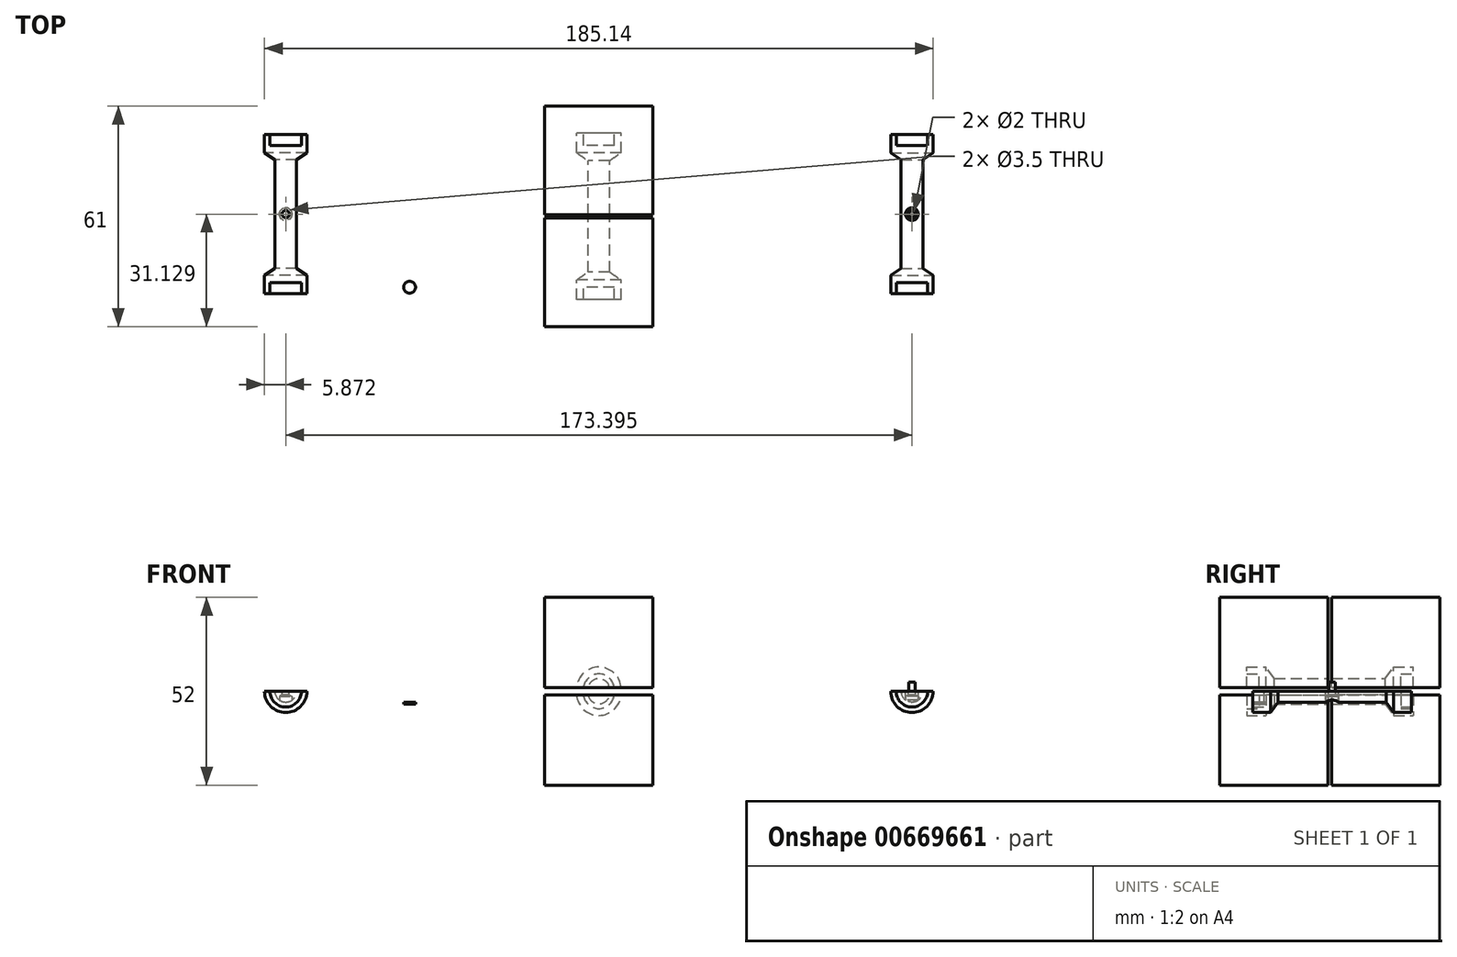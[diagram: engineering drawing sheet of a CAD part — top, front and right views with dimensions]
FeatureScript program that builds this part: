
annotation { "Feature Type Name" : "Feature", "Feature Type Description" : "" }
export const myFeature = defineFeature(function(context is Context, id is Id, definition is map)
    precondition{}
    {
        {
            var Q0;
            Q0=qCreatedBy(makeId("Top.planeOp"),FACE);
            var sketch = newSketch(context, id + "F0", { "sketchPlane" : qUnion([Q0])});
            skLineSegment(sketch, "E0", {"start": v(0, 71.15) * mm, "end": v(0, -54.04) * mm});
            skLineSegment(sketch, "E1", {"start": v(0, -54.04) * mm, "end": v(0, 71.15) * mm});
            skLineSegment(sketch, "E2", {"start": v(-3, 0) * mm, "end": v(-3, 15.4) * mm});
            skLineSegment(sketch, "E3", {"start": v(-3, 15.4) * mm, "end": v(-6.2, 17.63) * mm});
            skLineSegment(sketch, "E4", {"start": v(-6.2, 17.63) * mm, "end": v(-6.2, 23.03) * mm});
            skLineSegment(sketch, "E5", {"start": v(-6.2, 23.03) * mm, "end": v(-4.3, 23.03) * mm});
            skLineSegment(sketch, "E6", {"start": v(-4.3, 23.03) * mm, "end": v(-4.3, 19.63) * mm});
            skLineSegment(sketch, "E7", {"start": v(-4.3, 19.63) * mm, "end": v(0, 19.63) * mm});
            skLineSegment(sketch, "E8", {"start": v(0, 19.63) * mm, "end": v(0, 0) * mm});
            skLineSegment(sketch, "E9", {"start": v(0, 0) * mm, "end": v(-3, 0) * mm});
            skLineSegment(sketch, "E10.MirrorCS", {"start": v(-6.2, -23.03) * mm, "end": v(-4.3, -23.03) * mm});
            skLineSegment(sketch, "E11.MirrorCS", {"start": v(-3, -15.4) * mm, "end": v(-6.2, -17.63) * mm});
            skLineSegment(sketch, "E12.MirrorCS", {"start": v(-4.3, -23.03) * mm, "end": v(-4.3, -19.63) * mm});
            skLineSegment(sketch, "E13.MirrorCS", {"start": v(0, -19.63) * mm, "end": v(0, 0) * mm});
            skLineSegment(sketch, "E14.MirrorCS", {"start": v(-4.3, -19.63) * mm, "end": v(0, -19.63) * mm});
            skLineSegment(sketch, "E15.MirrorCS", {"start": v(-6.2, -17.63) * mm, "end": v(-6.2, -23.03) * mm});
            skLineSegment(sketch, "E16.MirrorCS", {"start": v(-3, 0) * mm, "end": v(-3, -15.4) * mm});
            skLineSegment(sketch, "E17", {"start": v(-89.7, 0.63) * mm, "end": v(-89.7, 15.63) * mm});
            skLineSegment(sketch, "E18", {"start": v(-89.7, 15.63) * mm, "end": v(-92.57, 17.63) * mm});
            skLineSegment(sketch, "E19", {"start": v(-92.57, 17.63) * mm, "end": v(-92.57, 22.63) * mm});
            skLineSegment(sketch, "E20", {"start": v(-92.57, 22.63) * mm, "end": v(-91.07, 22.63) * mm});
            skLineSegment(sketch, "E21", {"start": v(-91.07, 22.63) * mm, "end": v(-91.07, 19.63) * mm});
            skLineSegment(sketch, "E22", {"start": v(-91.07, 19.63) * mm, "end": v(-86.7, 19.63) * mm});
            skLineSegment(sketch, "E23", {"start": v(-86.7, 19.63) * mm, "end": v(-86.7, 0.63) * mm});
            skLineSegment(sketch, "E24", {"start": v(-86.7, 0.63) * mm, "end": v(-89.7, 0.63) * mm});
            skLineSegment(sketch, "E25.MirrorCS", {"start": v(-92.57, -21.37) * mm, "end": v(-91.07, -21.37) * mm});
            skLineSegment(sketch, "E26.MirrorCS", {"start": v(-89.7, -14.37) * mm, "end": v(-92.57, -16.37) * mm});
            skLineSegment(sketch, "E27.MirrorCS", {"start": v(-91.07, -21.37) * mm, "end": v(-91.07, -18.37) * mm});
            skLineSegment(sketch, "E28.MirrorCS", {"start": v(-92.57, -16.37) * mm, "end": v(-92.57, -21.37) * mm});
            skLineSegment(sketch, "E29.MirrorCS", {"start": v(-86.7, -18.37) * mm, "end": v(-86.7, 0.63) * mm});
            skLineSegment(sketch, "E30.MirrorCS", {"start": v(-91.07, -18.37) * mm, "end": v(-86.7, -18.37) * mm});
            skLineSegment(sketch, "E31.MirrorCS", {"start": v(-89.7, 0.63) * mm, "end": v(-89.7, -14.37) * mm});
            skSolve(sketch);
        }
        {
            var Q0;
            Q0=makeQuery(id+"F0.imprint","IMPRINT",FACE,{"disambiguationData":[TD([[makeQuery(id+"F0.imprint","IMPRINT",EDGE,{"derivedFrom":sQuery(id+"F0.wireOp",EDGE,"E2")}),-1.0]])]});
            var Q1;
            Q1=makeQuery(id+"F0.imprint","IMPRINT",FACE,{"disambiguationData":[TD([[makeQuery(id+"F0.imprint","IMPRINT",EDGE,{"derivedFrom":sQuery(id+"F0.wireOp",EDGE,"E10.MirrorCS")}),1.0]])]});
            var Q2;
            Q2=sQuery(id+"F0.wireOp",EDGE,"E8");
            revolve(context, id + "F1", {"entities" : qUnion([Q0, Q1]), "axis" : qUnion([Q2]), "revolveType" : RevolveType.ONE_DIRECTION, "angle" : 180 * degree});
        }
        {
            var Q0;
            Q0=qCreatedBy(makeId("Right.planeOp"),FACE);
            var sketch = newSketch(context, id + "F2", { "sketchPlane" : qUnion([Q0])});
            skLineSegment(sketch, "E32.bottom", {"start": v(30, -25) * mm, "end": v(0, -25) * mm});
            skLineSegment(sketch, "E32.top", {"start": v(30, -50) * mm, "end": v(0, -50) * mm});
            skLineSegment(sketch, "E32.left", {"start": v(30, -25) * mm, "end": v(30, -50) * mm});
            skLineSegment(sketch, "E32.right", {"start": v(0, -25) * mm, "end": v(0, -50) * mm});
            skSolve(sketch);
        }
        {
            var Q0;
            Q0=makeQuery(id+"F2.imprint","IMPRINT",FACE,{"disambiguationData":[TD([[makeQuery(id+"F2.imprint","IMPRINT",EDGE,{"derivedFrom":sQuery(id+"F2.wireOp",EDGE,"E32.bottom")}),1.0]])]});
            extrude(context, id + "F3", {"entities" : qUnion([Q0]), "depth" : 15 * mm, "offsetDistance" : 25 * mm, "hasSecondDirection" : true, "secondDirectionOppositeDirection" : true, "secondDirectionDepth" : 15 * mm});
        }
        {
            var Q0;
            Q0=makeQuery(id+"F1.opRevolve","SWEPT_BODY",BODY,{"disambiguationData":[OSD([sQuery(id+"F0.wireOp",EDGE,"E2"),sQuery(id+"F0.wireOp",EDGE,"E3"),sQuery(id+"F0.wireOp",EDGE,"E4"),sQuery(id+"F0.wireOp",EDGE,"E5"),sQuery(id+"F0.wireOp",EDGE,"E6"),sQuery(id+"F0.wireOp",EDGE,"E7"),sQuery(id+"F0.wireOp",EDGE,"E8"),sQuery(id+"F0.wireOp",EDGE,"E10.MirrorCS"),sQuery(id+"F0.wireOp",EDGE,"E11.MirrorCS"),sQuery(id+"F0.wireOp",EDGE,"E12.MirrorCS"),sQuery(id+"F0.wireOp",EDGE,"E13.MirrorCS"),sQuery(id+"F0.wireOp",EDGE,"E14.MirrorCS"),sQuery(id+"F0.wireOp",EDGE,"E15.MirrorCS"),sQuery(id+"F0.wireOp",EDGE,"E16.MirrorCS")])]});
            transform(context, id + "F4", {"entities" : qUnion([Q0]), "transformType" : TransformType.TRANSLATION_3D, "dx" : 0 * mm, "dy" : 0 * mm, "dz" : -24.5 * mm, "makeCopy" : false});
        }
        {
            var Q0;
            Q0=makeQuery(id+"F3.opExtrude","SWEPT_BODY",BODY,{"disambiguationData":[OSD([sQuery(id+"F2.wireOp",EDGE,"E32.bottom"),sQuery(id+"F2.wireOp",EDGE,"E32.top"),sQuery(id+"F2.wireOp",EDGE,"E32.left"),sQuery(id+"F2.wireOp",EDGE,"E32.right")])]});
            var Q1;
            Q1=qCreatedBy(makeId("Front.planeOp"),FACE);
            mirror(context, id + "F5", {"entities" : qUnion([Q0]), "mirrorPlane" : qUnion([Q1])});
        }
        {
            var Q0;
            Q0=makeQuery(id+"F3.opExtrude","SWEPT_BODY",BODY,{"disambiguationData":[OSD([sQuery(id+"F2.wireOp",EDGE,"E32.bottom"),sQuery(id+"F2.wireOp",EDGE,"E32.top"),sQuery(id+"F2.wireOp",EDGE,"E32.left"),sQuery(id+"F2.wireOp",EDGE,"E32.right")])]});
            transform(context, id + "F6", {"entities" : qUnion([Q0]), "transformType" : TransformType.TRANSLATION_3D, "dx" : 0 * mm, "dy" : .5 * mm, "dz" : 0 * mm, "makeCopy" : false});
        }
        {
            var Q0;
            Q0=makeQuery(id+"F5.opPattern","COPY",BODY,{"derivedFrom":makeQuery(id+"F3.opExtrude","SWEPT_BODY",BODY,{"disambiguationData":[OSD([sQuery(id+"F2.wireOp",EDGE,"E32.bottom"),sQuery(id+"F2.wireOp",EDGE,"E32.top"),sQuery(id+"F2.wireOp",EDGE,"E32.left"),sQuery(id+"F2.wireOp",EDGE,"E32.right")])]}),"instanceName":"1"});
            transform(context, id + "F7", {"entities" : qUnion([Q0]), "transformType" : TransformType.TRANSLATION_3D, "dx" : 0 * mm, "dy" : -.5 * mm, "dz" : 0 * mm, "makeCopy" : false});
        }
        {
            var Q0;
            Q0=makeQuery(id+"F1.opRevolve","SWEPT_BODY",BODY,{"disambiguationData":[OSD([sQuery(id+"F0.wireOp",EDGE,"E2"),sQuery(id+"F0.wireOp",EDGE,"E3"),sQuery(id+"F0.wireOp",EDGE,"E4"),sQuery(id+"F0.wireOp",EDGE,"E5"),sQuery(id+"F0.wireOp",EDGE,"E6"),sQuery(id+"F0.wireOp",EDGE,"E7"),sQuery(id+"F0.wireOp",EDGE,"E8"),sQuery(id+"F0.wireOp",EDGE,"E10.MirrorCS"),sQuery(id+"F0.wireOp",EDGE,"E11.MirrorCS"),sQuery(id+"F0.wireOp",EDGE,"E12.MirrorCS"),sQuery(id+"F0.wireOp",EDGE,"E13.MirrorCS"),sQuery(id+"F0.wireOp",EDGE,"E14.MirrorCS"),sQuery(id+"F0.wireOp",EDGE,"E15.MirrorCS"),sQuery(id+"F0.wireOp",EDGE,"E16.MirrorCS")])]});
            var Q1;
            Q1=makeQuery(id+"F5.opPattern","COPY",BODY,{"derivedFrom":makeQuery(id+"F3.opExtrude","SWEPT_BODY",BODY,{"disambiguationData":[OSD([sQuery(id+"F2.wireOp",EDGE,"E32.bottom"),sQuery(id+"F2.wireOp",EDGE,"E32.top"),sQuery(id+"F2.wireOp",EDGE,"E32.left"),sQuery(id+"F2.wireOp",EDGE,"E32.right")])]}),"instanceName":"1"});
            var Q2;
            Q2=makeQuery(id+"F3.opExtrude","SWEPT_BODY",BODY,{"disambiguationData":[OSD([sQuery(id+"F2.wireOp",EDGE,"E32.bottom"),sQuery(id+"F2.wireOp",EDGE,"E32.top"),sQuery(id+"F2.wireOp",EDGE,"E32.left"),sQuery(id+"F2.wireOp",EDGE,"E32.right")])]});
            var Q3;
            Q3=qCreatedBy(makeId("Top.planeOp"),FACE);
            mirror(context, id + "F8", {"entities" : qUnion([Q0, Q1, Q2]), "mirrorPlane" : qUnion([Q3])});
        }
        {
            var Q0;
            Q0=makeQuery(id+"F1.opRevolve","SWEPT_BODY",BODY,{"disambiguationData":[OSD([sQuery(id+"F0.wireOp",EDGE,"E2"),sQuery(id+"F0.wireOp",EDGE,"E3"),sQuery(id+"F0.wireOp",EDGE,"E4"),sQuery(id+"F0.wireOp",EDGE,"E5"),sQuery(id+"F0.wireOp",EDGE,"E6"),sQuery(id+"F0.wireOp",EDGE,"E7"),sQuery(id+"F0.wireOp",EDGE,"E8"),sQuery(id+"F0.wireOp",EDGE,"E10.MirrorCS"),sQuery(id+"F0.wireOp",EDGE,"E11.MirrorCS"),sQuery(id+"F0.wireOp",EDGE,"E12.MirrorCS"),sQuery(id+"F0.wireOp",EDGE,"E13.MirrorCS"),sQuery(id+"F0.wireOp",EDGE,"E14.MirrorCS"),sQuery(id+"F0.wireOp",EDGE,"E15.MirrorCS"),sQuery(id+"F0.wireOp",EDGE,"E16.MirrorCS")])]});
            var Q1;
            Q1=makeQuery(id+"F3.opExtrude","SWEPT_BODY",BODY,{"disambiguationData":[OSD([sQuery(id+"F2.wireOp",EDGE,"E32.bottom"),sQuery(id+"F2.wireOp",EDGE,"E32.top"),sQuery(id+"F2.wireOp",EDGE,"E32.left"),sQuery(id+"F2.wireOp",EDGE,"E32.right")])]});
            var Q2;
            Q2=makeQuery(id+"F5.opPattern","COPY",BODY,{"derivedFrom":makeQuery(id+"F3.opExtrude","SWEPT_BODY",BODY,{"disambiguationData":[OSD([sQuery(id+"F2.wireOp",EDGE,"E32.bottom"),sQuery(id+"F2.wireOp",EDGE,"E32.top"),sQuery(id+"F2.wireOp",EDGE,"E32.left"),sQuery(id+"F2.wireOp",EDGE,"E32.right")])]}),"instanceName":"1"});
            booleanBodies(context, id + "F9", {"operationType" : BooleanOperationType.SUBTRACTION, "tools" : qUnion([Q0]), "targets" : qUnion([Q1, Q2])});
        }
        {
            var Q0;
            Q0=makeQuery(id+"F8.opPattern","COPY",BODY,{"derivedFrom":makeQuery(id+"F1.opRevolve","SWEPT_BODY",BODY,{"disambiguationData":[OSD([sQuery(id+"F0.wireOp",EDGE,"E2"),sQuery(id+"F0.wireOp",EDGE,"E3"),sQuery(id+"F0.wireOp",EDGE,"E4"),sQuery(id+"F0.wireOp",EDGE,"E5"),sQuery(id+"F0.wireOp",EDGE,"E6"),sQuery(id+"F0.wireOp",EDGE,"E7"),sQuery(id+"F0.wireOp",EDGE,"E8"),sQuery(id+"F0.wireOp",EDGE,"E10.MirrorCS"),sQuery(id+"F0.wireOp",EDGE,"E11.MirrorCS"),sQuery(id+"F0.wireOp",EDGE,"E12.MirrorCS"),sQuery(id+"F0.wireOp",EDGE,"E13.MirrorCS"),sQuery(id+"F0.wireOp",EDGE,"E14.MirrorCS"),sQuery(id+"F0.wireOp",EDGE,"E15.MirrorCS"),sQuery(id+"F0.wireOp",EDGE,"E16.MirrorCS")])]}),"instanceName":"1"});
            var Q1;
            Q1=makeQuery(id+"F8.opPattern","COPY",BODY,{"derivedFrom":makeQuery(id+"F3.opExtrude","SWEPT_BODY",BODY,{"disambiguationData":[OSD([sQuery(id+"F2.wireOp",EDGE,"E32.bottom"),sQuery(id+"F2.wireOp",EDGE,"E32.top"),sQuery(id+"F2.wireOp",EDGE,"E32.left"),sQuery(id+"F2.wireOp",EDGE,"E32.right")])]}),"instanceName":"1"});
            var Q2;
            Q2=makeQuery(id+"F8.opPattern","COPY",BODY,{"derivedFrom":makeQuery(id+"F5.opPattern","COPY",BODY,{"derivedFrom":makeQuery(id+"F3.opExtrude","SWEPT_BODY",BODY,{"disambiguationData":[OSD([sQuery(id+"F2.wireOp",EDGE,"E32.bottom"),sQuery(id+"F2.wireOp",EDGE,"E32.top"),sQuery(id+"F2.wireOp",EDGE,"E32.left"),sQuery(id+"F2.wireOp",EDGE,"E32.right")])]}),"instanceName":"1"}),"instanceName":"1"});
            booleanBodies(context, id + "F10", {"operationType" : BooleanOperationType.SUBTRACTION, "tools" : qUnion([Q0]), "targets" : qUnion([Q1, Q2])});
        }
        {
            var Q0;
            Q0=makeQuery(id+"F8.opPattern","COPY",BODY,{"derivedFrom":makeQuery(id+"F5.opPattern","COPY",BODY,{"derivedFrom":makeQuery(id+"F3.opExtrude","SWEPT_BODY",BODY,{"disambiguationData":[OSD([sQuery(id+"F2.wireOp",EDGE,"E32.bottom"),sQuery(id+"F2.wireOp",EDGE,"E32.top"),sQuery(id+"F2.wireOp",EDGE,"E32.left"),sQuery(id+"F2.wireOp",EDGE,"E32.right")])]}),"instanceName":"1"}),"instanceName":"1"});
            var Q1;
            Q1=makeQuery(id+"F8.opPattern","COPY",BODY,{"derivedFrom":makeQuery(id+"F3.opExtrude","SWEPT_BODY",BODY,{"disambiguationData":[OSD([sQuery(id+"F2.wireOp",EDGE,"E32.bottom"),sQuery(id+"F2.wireOp",EDGE,"E32.top"),sQuery(id+"F2.wireOp",EDGE,"E32.left"),sQuery(id+"F2.wireOp",EDGE,"E32.right")])]}),"instanceName":"1"});
            transform(context, id + "F11", {"entities" : qUnion([Q0, Q1]), "transformType" : TransformType.TRANSLATION_3D, "dx" : 0 * mm, "dy" : 0 * mm, "dz" : -24 * mm, "makeCopy" : false});
        }
        {
            var Q0;
            Q0=makeQuery(id+"F3.opExtrude","SWEPT_BODY",BODY,{"disambiguationData":[OSD([sQuery(id+"F2.wireOp",EDGE,"E32.bottom"),sQuery(id+"F2.wireOp",EDGE,"E32.top"),sQuery(id+"F2.wireOp",EDGE,"E32.left"),sQuery(id+"F2.wireOp",EDGE,"E32.right")])]});
            var Q1;
            Q1=makeQuery(id+"F5.opPattern","COPY",BODY,{"derivedFrom":makeQuery(id+"F3.opExtrude","SWEPT_BODY",BODY,{"disambiguationData":[OSD([sQuery(id+"F2.wireOp",EDGE,"E32.bottom"),sQuery(id+"F2.wireOp",EDGE,"E32.top"),sQuery(id+"F2.wireOp",EDGE,"E32.left"),sQuery(id+"F2.wireOp",EDGE,"E32.right")])]}),"instanceName":"1"});
            transform(context, id + "F12", {"entities" : qUnion([Q0, Q1]), "transformType" : TransformType.TRANSLATION_3D, "dx" : 0 * mm, "dy" : 0 * mm, "dz" : 24 * mm, "makeCopy" : false});
        }
        {
            var Q0;
            Q0=makeQuery(id+"F0.imprint","IMPRINT",FACE,{"disambiguationData":[TD([[makeQuery(id+"F0.imprint","IMPRINT",EDGE,{"derivedFrom":sQuery(id+"F0.wireOp",EDGE,"E17")}),-1.0]])]});
            var Q1;
            Q1=makeQuery(id+"F0.imprint","IMPRINT",FACE,{"disambiguationData":[TD([[makeQuery(id+"F0.imprint","IMPRINT",EDGE,{"derivedFrom":sQuery(id+"F0.wireOp",EDGE,"E24")}),1.0]])]});
            var Q2;
            Q2=sQuery(id+"F0.wireOp",EDGE,"E23");
            revolve(context, id + "F13", {"entities" : qUnion([Q0, Q1]), "axis" : qUnion([Q2]), "revolveType" : RevolveType.ONE_DIRECTION, "angle" : 180 * degree});
        }
        {
            var Q0;
            Q0=sQuery(id+"F0.wireOp",VERTEX,"E24.start");
            var Q1;
            Q1=makeQuery(id+"F13.opRevolve","SWEPT_BODY",BODY,{"disambiguationData":[OSD([sQuery(id+"F0.wireOp",EDGE,"E17"),sQuery(id+"F0.wireOp",EDGE,"E18"),sQuery(id+"F0.wireOp",EDGE,"E19"),sQuery(id+"F0.wireOp",EDGE,"E20"),sQuery(id+"F0.wireOp",EDGE,"E21"),sQuery(id+"F0.wireOp",EDGE,"E22"),sQuery(id+"F0.wireOp",EDGE,"E23"),sQuery(id+"F0.wireOp",EDGE,"E25.MirrorCS"),sQuery(id+"F0.wireOp",EDGE,"E26.MirrorCS"),sQuery(id+"F0.wireOp",EDGE,"E27.MirrorCS"),sQuery(id+"F0.wireOp",EDGE,"E28.MirrorCS"),sQuery(id+"F0.wireOp",EDGE,"E29.MirrorCS"),sQuery(id+"F0.wireOp",EDGE,"E30.MirrorCS"),sQuery(id+"F0.wireOp",EDGE,"E31.MirrorCS")])]});
            hole(context, id + "F14", {"style" : HoleStyle.SIMPLE, "endStyle" : HoleEndStyle.THROUGH, "holeDiameter" : 2 * mm, "majorDiameter" : 5 * mm, "isTappedThrough" : true, "tappedDepth" : 12 * mm, "tapClearance" : 3, "locations" : qUnion([Q0]), "scope" : qUnion([Q1])});
        }
        {
            var Q0;
            Q0=qCreatedBy(makeId("Top.planeOp"),FACE);
            cPlane(context, id + "F15", {"entities" : qUnion([Q0]), "cplaneType" : CPlaneType.OFFSET, "offset" : 3.01 * mm, "oppositeDirection" : true, "width" : 150 * mm, "height" : 150 * mm});
        }
        {
            var Q0;
            Q0=qCreatedBy(id+"F15.planeOp",FACE);
            var sketch = newSketch(context, id + "F16", { "sketchPlane" : qUnion([Q0])});
            skCircle(sketch, "E33", {"center": v(-86.7, 0.63) * mm, "radius": 1.75 * mm});
            skSolve(sketch);
        }
        {
            var Q0;
            Q0=sQuery(id+"F16.wireOp",VERTEX,"E33.center");
            var Q1;
            Q1=makeQuery(id+"F13.opRevolve","SWEPT_BODY",BODY,{"disambiguationData":[OSD([sQuery(id+"F0.wireOp",EDGE,"E17"),sQuery(id+"F0.wireOp",EDGE,"E18"),sQuery(id+"F0.wireOp",EDGE,"E19"),sQuery(id+"F0.wireOp",EDGE,"E20"),sQuery(id+"F0.wireOp",EDGE,"E21"),sQuery(id+"F0.wireOp",EDGE,"E22"),sQuery(id+"F0.wireOp",EDGE,"E23"),sQuery(id+"F0.wireOp",EDGE,"E25.MirrorCS"),sQuery(id+"F0.wireOp",EDGE,"E26.MirrorCS"),sQuery(id+"F0.wireOp",EDGE,"E27.MirrorCS"),sQuery(id+"F0.wireOp",EDGE,"E28.MirrorCS"),sQuery(id+"F0.wireOp",EDGE,"E29.MirrorCS"),sQuery(id+"F0.wireOp",EDGE,"E30.MirrorCS"),sQuery(id+"F0.wireOp",EDGE,"E31.MirrorCS")])]});
            hole(context, id + "F17", {"style" : HoleStyle.SIMPLE, "endStyle" : HoleEndStyle.BLIND, "oppositeDirection" : true, "holeDiameter" : 3.5 * mm, "majorDiameter" : 5 * mm, "holeDepth" : 1 * mm, "isTappedThrough" : true, "tappedDepth" : 12 * mm, "tapClearance" : 3, "locations" : qUnion([Q0]), "scope" : qUnion([Q1])});
        }
        {
            var Q0;
            Q0=makeQuery(id+"F13.opRevolve","SWEPT_BODY",BODY,{"disambiguationData":[OSD([sQuery(id+"F0.wireOp",EDGE,"E17"),sQuery(id+"F0.wireOp",EDGE,"E18"),sQuery(id+"F0.wireOp",EDGE,"E19"),sQuery(id+"F0.wireOp",EDGE,"E20"),sQuery(id+"F0.wireOp",EDGE,"E21"),sQuery(id+"F0.wireOp",EDGE,"E22"),sQuery(id+"F0.wireOp",EDGE,"E23"),sQuery(id+"F0.wireOp",EDGE,"E25.MirrorCS"),sQuery(id+"F0.wireOp",EDGE,"E26.MirrorCS"),sQuery(id+"F0.wireOp",EDGE,"E27.MirrorCS"),sQuery(id+"F0.wireOp",EDGE,"E28.MirrorCS"),sQuery(id+"F0.wireOp",EDGE,"E29.MirrorCS"),sQuery(id+"F0.wireOp",EDGE,"E30.MirrorCS"),sQuery(id+"F0.wireOp",EDGE,"E31.MirrorCS")])]});
            var Q1;
            Q1=qCreatedBy(makeId("Right.planeOp"),FACE);
            mirror(context, id + "F18", {"entities" : qUnion([Q0]), "mirrorPlane" : qUnion([Q1])});
        }
        {
            var Q0;
            Q0=qCreatedBy(makeId("Top.planeOp"),FACE);
            var sketch = newSketch(context, id + "F19", { "sketchPlane" : qUnion([Q0])});
            skCircle(sketch, "E34", {"center": v(86.7, 0.63) * mm, "radius": 0.85 * mm});
            skCircle(sketch, "E35", {"center": v(86.7, 0.63) * mm, "radius": 1.75 * mm});
            skSolve(sketch);
        }
        {
            var Q0;
            Q0=makeQuery(id+"F19.imprint","IMPRINT",FACE,{"disambiguationData":[TD([[makeQuery(id+"F19.imprint","IMPRINT",EDGE,{"derivedFrom":sQuery(id+"F19.wireOp",EDGE,"E34")}),1.0]])]});
            extrude(context, id + "F20", {"entities" : qUnion([Q0]), "operationType" : NewBodyOperationType.ADD, "depth" : 2.5 * mm, "offsetDistance" : 25 * mm});
        }
        {
            var Q0;
            Q0=makeQuery(id+"F19.imprint","IMPRINT",FACE,{"disambiguationData":[TD([[makeQuery(id+"F19.imprint","IMPRINT",EDGE,{"derivedFrom":sQuery(id+"F19.wireOp",EDGE,"E34")}),-1.0]])]});
            var Q1;
            Q1=makeQuery(id+"F19.imprint","IMPRINT",FACE,{"disambiguationData":[TD([[makeQuery(id+"F19.imprint","IMPRINT",EDGE,{"derivedFrom":sQuery(id+"F19.wireOp",EDGE,"E34")}),1.0]])]});
            extrude(context, id + "F21", {"entities" : qUnion([Q0, Q1]), "oppositeDirection" : true, "depth" : 2.4 * mm, "offsetDistance" : 25 * mm});
        }
        {
            var Q0;
            Q0=qCreatedBy(id+"F15.planeOp",FACE);
            var sketch = newSketch(context, id + "F22", { "sketchPlane" : qUnion([Q0])});
            skCircle(sketch, "E36", {"center": v(-52.4, -19.62) * mm, "radius": 1.65 * mm});
            skSolve(sketch);
        }
        {
            var Q0;
            Q0=makeQuery(id+"F22.imprint","IMPRINT",FACE,{"disambiguationData":[TD([[makeQuery(id+"F22.imprint","IMPRINT",EDGE,{"derivedFrom":sQuery(id+"F22.wireOp",EDGE,"E36")}),1.0]])]});
            extrude(context, id + "F23", {"entities" : qUnion([Q0]), "oppositeDirection" : true, "depth" : .5 * mm, "offsetDistance" : 25 * mm});
        }
    });
